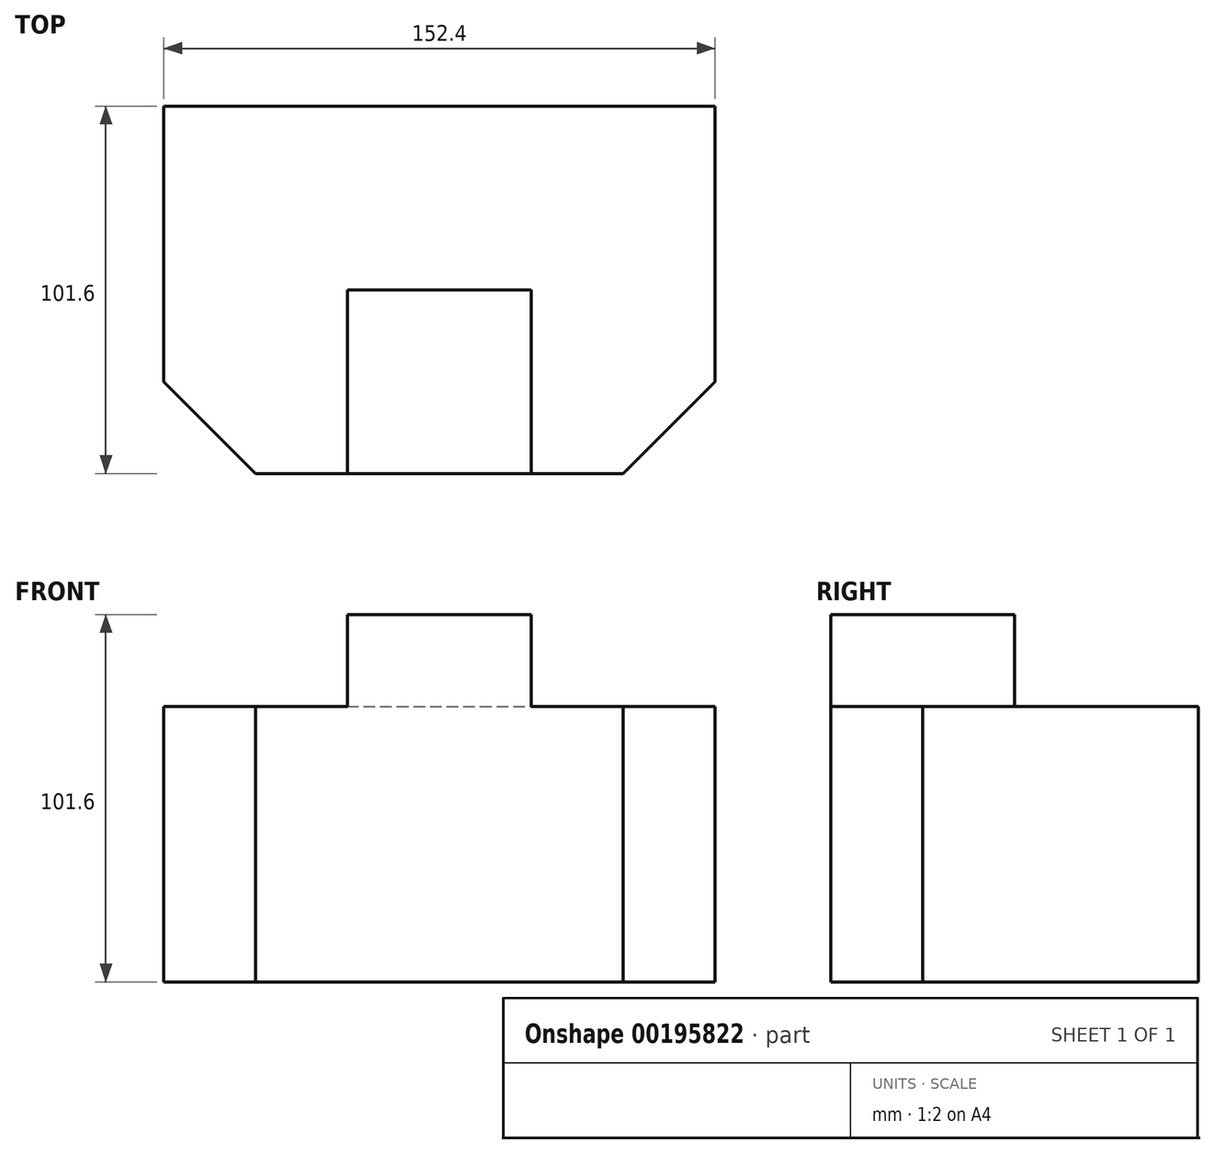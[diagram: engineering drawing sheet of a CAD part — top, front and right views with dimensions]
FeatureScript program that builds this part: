
annotation { "Feature Type Name" : "Feature", "Feature Type Description" : "" }
export const myFeature = defineFeature(function(context is Context, id is Id, definition is map)
    precondition{}
    {
        {
            var Q0;
            Q0=qCreatedBy(makeId("Top.planeOp"),FACE);
            var sketch = newSketch(context, id + "F0", { "sketchPlane" : qUnion([Q0])});
            skLineSegment(sketch, "E0.bottom", {"start": v(-76.2, 50.8) * mm, "end": v(76.2, 50.8) * mm});
            skLineSegment(sketch, "E0.top", {"start": v(-76.2, -50.8) * mm, "end": v(76.2, -50.8) * mm});
            skLineSegment(sketch, "E0.left", {"start": v(-76.2, 50.8) * mm, "end": v(-76.2, -50.8) * mm});
            skLineSegment(sketch, "E0.right", {"start": v(76.2, 50.8) * mm, "end": v(76.2, -50.8) * mm});
            skPoint(sketch, "E0.middle", {"position": v(0, 0) * mm});
            skLineSegment(sketch, "E1", {"start": v(-76.2, -25.4) * mm, "end": v(-50.8, -50.8) * mm});
            skLineSegment(sketch, "E2", {"start": v(76.2, -25.4) * mm, "end": v(50.8, -50.8) * mm});
            skSolve(sketch);
        }
        {
            var Q0;
            {var subQ1=sQuery(id+"F0.wireOp",EDGE,"E0.bottom");Q0=makeQuery(id+"F0.imprint","IMPRINT",FACE,{"disambiguationData":[TD([[makeQuery(id+"F0.imprint","IMPRINT",EDGE,{"derivedFrom":subQ1}),-1.0]])]});}
            extrude(context, id + "F1", {"entities" : qUnion([Q0]), "depth" : 76.2 * mm});
        }
        {
            var Q0;
            Q0=qCreatedBy(makeId("Top.planeOp"),FACE);
            cPlane(context, id + "F2", {"entities" : qUnion([Q0]), "cplaneType" : CPlaneType.OFFSET, "offset" : 76.2 * mm, "width" : 152.4 * mm, "height" : 152.4 * mm});
        }
        {
            var Q0;
            Q0=qCreatedBy(id+"F2.planeOp",FACE);
            var sketch = newSketch(context, id + "F3", { "sketchPlane" : qUnion([Q0])});
            skLineSegment(sketch, "E3.bottom", {"start": v(-25.4, 0) * mm, "end": v(25.4, 0) * mm});
            skLineSegment(sketch, "E3.top", {"start": v(-25.4, -50.8) * mm, "end": v(25.4, -50.8) * mm});
            skLineSegment(sketch, "E3.left", {"start": v(-25.4, 0) * mm, "end": v(-25.4, -50.8) * mm});
            skLineSegment(sketch, "E3.right", {"start": v(25.4, 0) * mm, "end": v(25.4, -50.8) * mm});
            skPoint(sketch, "E3.middle", {"position": v(0, -25.4) * mm});
            skSolve(sketch);
        }
        {
            var Q0;
            Q0=makeQuery(id+"F3.imprint","IMPRINT",FACE,{"disambiguationData":[TD([[makeQuery(id+"F3.imprint","IMPRINT",EDGE,{"derivedFrom":sQuery(id+"F3.wireOp",EDGE,"E3.bottom")}),-1.0]])]});
            extrude(context, id + "F4", {"entities" : qUnion([Q0]), "operationType" : NewBodyOperationType.ADD, "depth" : 25.4 * mm});
        }
    });
